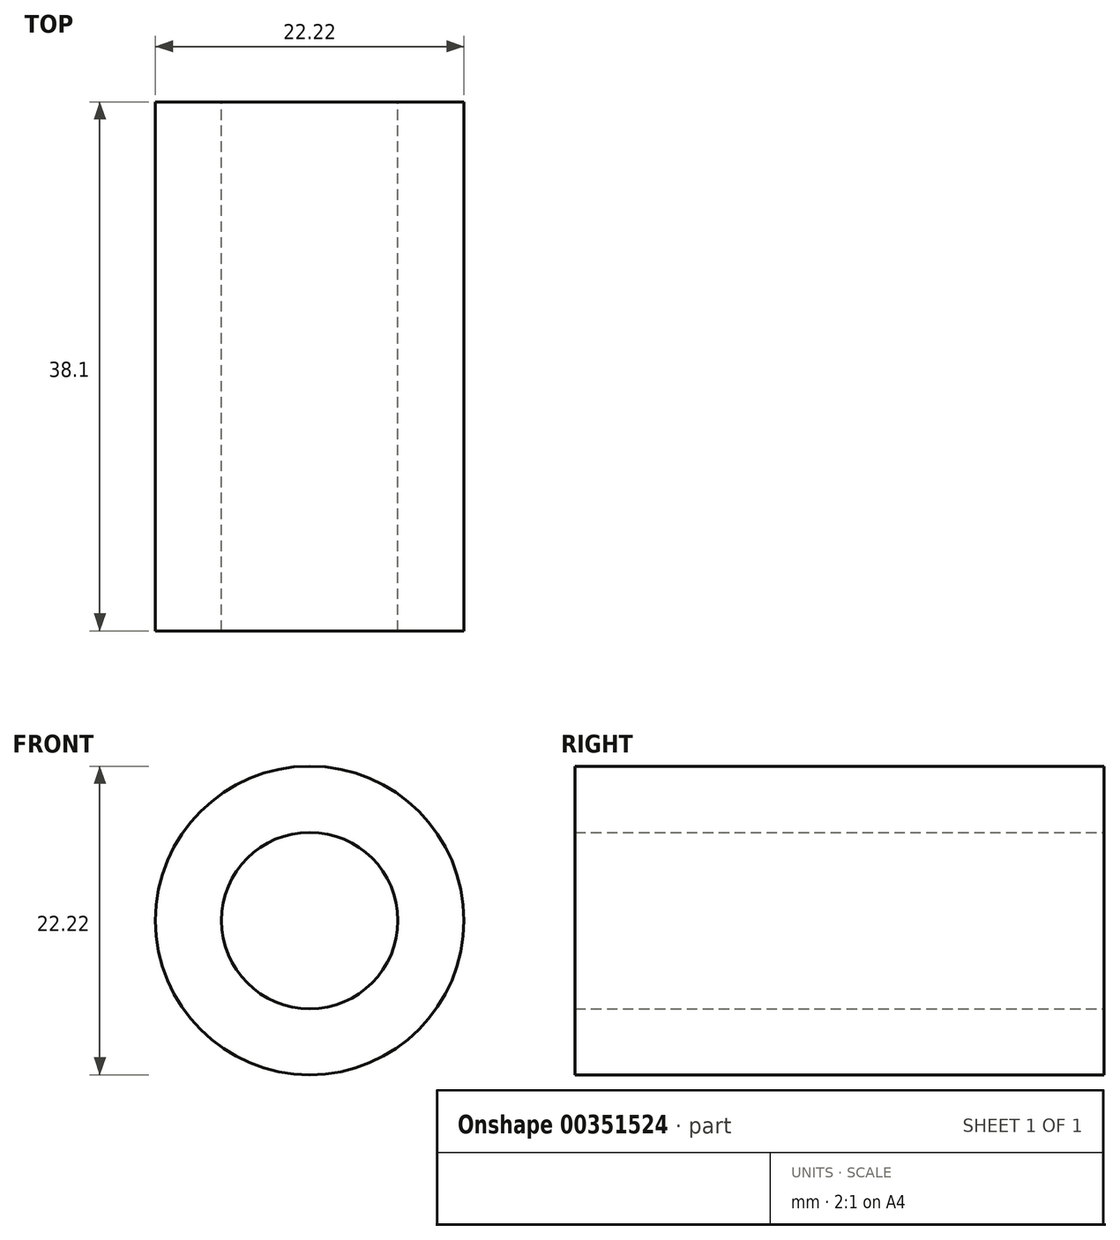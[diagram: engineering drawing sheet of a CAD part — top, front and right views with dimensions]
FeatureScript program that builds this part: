
annotation { "Feature Type Name" : "Feature", "Feature Type Description" : "" }
export const myFeature = defineFeature(function(context is Context, id is Id, definition is map)
    precondition{}
    {
        {
            var Q0;
            Q0=qCreatedBy(makeId("Front.planeOp"),FACE);
            var sketch = newSketch(context, id + "F0", { "sketchPlane" : qUnion([Q0])});
            skCircle(sketch, "E0", {"center": v(0, 0) * mm, "radius": 11.11 * mm});
            skCircle(sketch, "E1", {"center": v(0, 0) * mm, "radius": 6.35 * mm});
            skSolve(sketch);
        }
        {
            var Q0;
            Q0 = qSketchRegion(id + "F0", true);
            extrude(context, id + "F1", {"entities" : qUnion([Q0]), "depth" : 38.1 * mm, "symmetric" : true});
        }
    });
